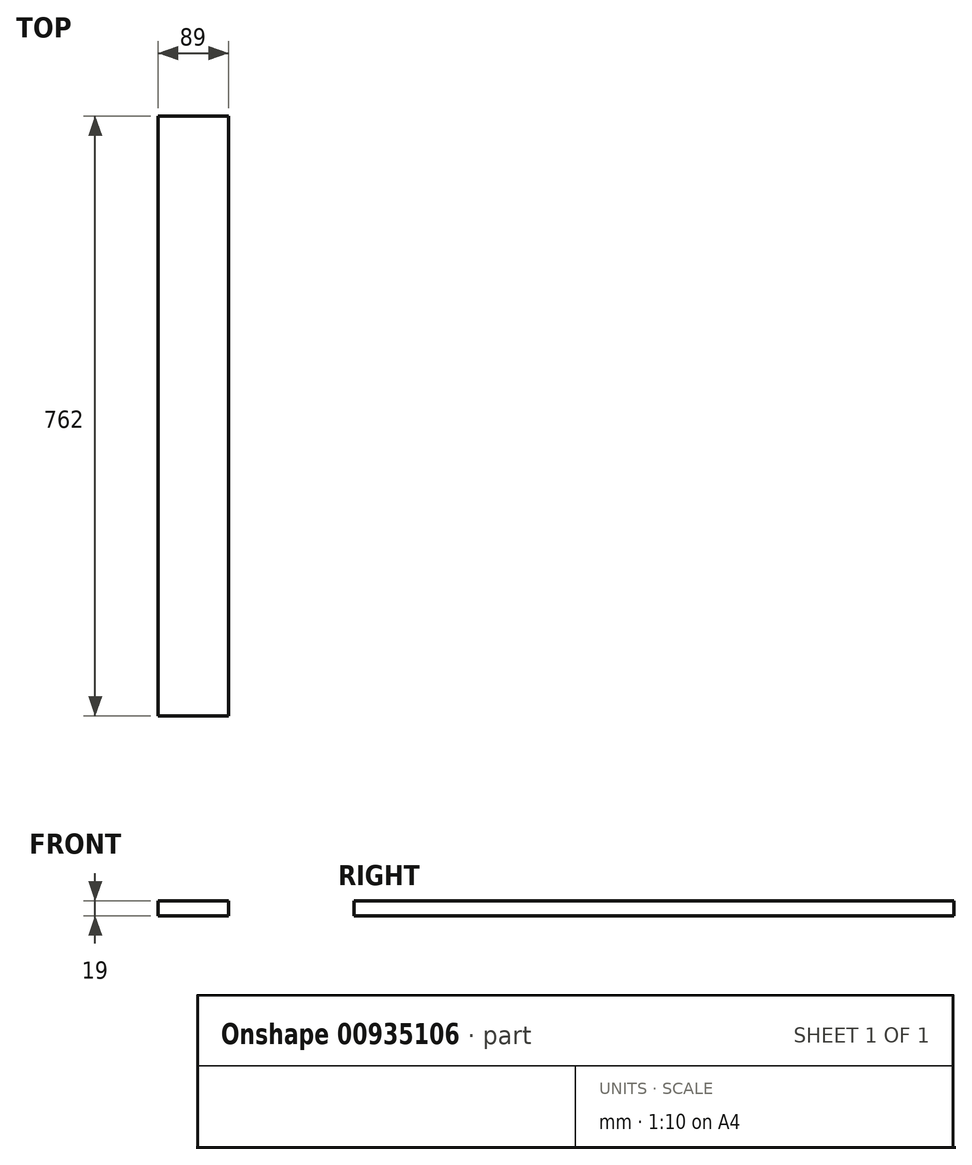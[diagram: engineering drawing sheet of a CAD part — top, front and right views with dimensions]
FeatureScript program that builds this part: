
annotation { "Feature Type Name" : "Feature", "Feature Type Description" : "" }
export const myFeature = defineFeature(function(context is Context, id is Id, definition is map)
    precondition{}
    {
        {
            var Q0;
            Q0=qCreatedBy(makeId("Front.planeOp"),FACE);
            var sketch = newSketch(context, id + "F0", { "sketchPlane" : qUnion([Q0])});
            skLineSegment(sketch, "E0.bottom", {"start": v(0, 0) * mm, "end": v(89, 0) * mm});
            skLineSegment(sketch, "E0.top", {"start": v(0, 19) * mm, "end": v(89, 19) * mm});
            skLineSegment(sketch, "E0.left", {"start": v(0, 0) * mm, "end": v(0, 19) * mm});
            skLineSegment(sketch, "E0.right", {"start": v(89, 0) * mm, "end": v(89, 19) * mm});
            skSolve(sketch);
        }
        {
            var Q0;
            Q0=makeQuery(id+"F0.imprint","IMPRINT",FACE,{"disambiguationData":[TD([[makeQuery(id+"F0.imprint","IMPRINT",EDGE,{"derivedFrom":sQuery(id+"F0.wireOp",EDGE,"E0.bottom")}),1.0]])]});
            extrude(context, id + "F1", {"entities" : qUnion([Q0]), "depth" : 762 * mm, "offsetDistance" : 25 * mm});
        }
    });
